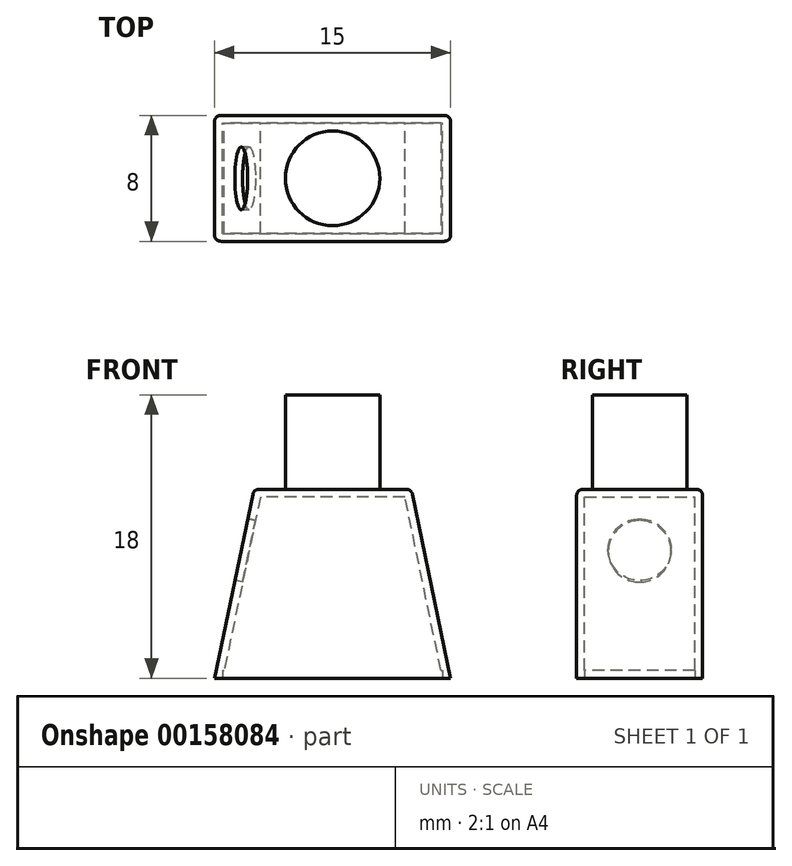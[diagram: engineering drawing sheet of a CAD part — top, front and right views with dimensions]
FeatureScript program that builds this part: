
annotation { "Feature Type Name" : "Feature", "Feature Type Description" : "" }
export const myFeature = defineFeature(function(context is Context, id is Id, definition is map)
    precondition{}
    {
        {
            var Q0;
            Q0=qCreatedBy(makeId("Front.planeOp"),FACE);
            var sketch = newSketch(context, id + "F0", { "sketchPlane" : qUnion([Q0])});
            skLineSegment(sketch, "E0", {"start": v(0, 0) * mm, "end": v(7.5, 0) * mm});
            skLineSegment(sketch, "E1", {"start": v(7.5, 0) * mm, "end": v(5, 12) * mm});
            skLineSegment(sketch, "E2", {"start": v(5, 12) * mm, "end": v(0, 12) * mm});
            skLineSegment(sketch, "E3", {"start": v(0, 12) * mm, "end": v(-5, 12) * mm});
            skLineSegment(sketch, "E4", {"start": v(-5, 12) * mm, "end": v(-7.5, 0) * mm});
            skLineSegment(sketch, "E5", {"start": v(-7.5, 0) * mm, "end": v(0, 0) * mm});
            skSolve(sketch);
        }
        {
            var Q0;
            Q0=makeQuery(id+"F0.imprint","IMPRINT",FACE,{"disambiguationData":[TD([[makeQuery(id+"F0.imprint","IMPRINT",EDGE,{"derivedFrom":sQuery(id+"F0.wireOp",EDGE,"E0")}),1.0]])]});
            extrude(context, id + "F1", {"entities" : qUnion([Q0]), "depth" : 8 * mm});
        }
        {
            var Q0;
            Q0=makeQuery(id+"F1.opExtrude","SWEPT_FACE",FACE,{"disambiguationData":[OSD([sQuery(id+"F0.wireOp",EDGE,"E0"),sQuery(id+"F0.wireOp",EDGE,"E5")])]});
            shell(context, id + "F2", {"entities" : qUnion([Q0]), "thickness" : 0.5 * mm});
        }
        {
            var Q0;
            Q0=makeQuery(id+"F1.opExtrude","SWEPT_FACE",FACE,{"disambiguationData":[OSD([sQuery(id+"F0.wireOp",EDGE,"E0"),sQuery(id+"F0.wireOp",EDGE,"E5")])]});
            var sketch = newSketch(context, id + "F3", { "sketchPlane" : qUnion([Q0])});
            skLineSegment(sketch, "E6.0", {"start": v(-6.99, 7.5) * mm, "end": v(6.99, 7.5) * mm});
            skLineSegment(sketch, "E7.0", {"start": v(-6.99, 7.5) * mm, "end": v(-6.99, 0.5) * mm});
            skLineSegment(sketch, "E8.0", {"start": v(-6.99, 0.5) * mm, "end": v(6.99, 0.5) * mm});
            skLineSegment(sketch, "E9.0", {"start": v(6.99, 7.5) * mm, "end": v(6.99, 0.5) * mm});
            skSolve(sketch);
        }
        {
            var Q0;
            Q0=makeQuery(id+"F3.imprint","IMPRINT",FACE,{"disambiguationData":[TD([[makeQuery(id+"F3.imprint","IMPRINT",EDGE,{"derivedFrom":sQuery(id+"F3.wireOp",EDGE,"E6.0")}),-1.0]])]});
            extrude(context, id + "F4", {"entities" : qUnion([Q0]), "operationType" : NewBodyOperationType.REMOVE, "oppositeDirection" : true, "depth" : 0.5 * mm});
        }
        {
            var Q0;
            Q0=makeQuery(id+"F1.opExtrude","CAP_EDGE",EDGE,{"disambiguationData":[OSD([sQuery(id+"F0.wireOp",EDGE,"E1")])],"isStart":false});
            var Q1;
            Q1=makeQuery(id+"F1.opExtrude","SWEPT_EDGE",EDGE,{"disambiguationData":[OSD([sQuery(id+"F0.wireOp",EDGE,"E1"),sQuery(id+"F0.wireOp",EDGE,"E2")])]});
            var Q2;
            Q2=makeQuery(id+"F1.opExtrude","CAP_EDGE",EDGE,{"disambiguationData":[OSD([sQuery(id+"F0.wireOp",EDGE,"E2"),sQuery(id+"F0.wireOp",EDGE,"E3")])],"isStart":false});
            var Q3;
            Q3=makeQuery(id+"F1.opExtrude","CAP_EDGE",EDGE,{"disambiguationData":[OSD([sQuery(id+"F0.wireOp",EDGE,"E1")])],"isStart":true});
            var Q4;
            Q4=makeQuery(id+"F1.opExtrude","CAP_EDGE",EDGE,{"disambiguationData":[OSD([sQuery(id+"F0.wireOp",EDGE,"E2"),sQuery(id+"F0.wireOp",EDGE,"E3")])],"isStart":true});
            var Q5;
            Q5=makeQuery(id+"F1.opExtrude","CAP_EDGE",EDGE,{"disambiguationData":[OSD([sQuery(id+"F0.wireOp",EDGE,"E4")])],"isStart":true});
            var Q6;
            Q6=makeQuery(id+"F1.opExtrude","SWEPT_EDGE",EDGE,{"disambiguationData":[OSD([sQuery(id+"F0.wireOp",EDGE,"E3"),sQuery(id+"F0.wireOp",EDGE,"E4")])]});
            var Q7;
            Q7=makeQuery(id+"F1.opExtrude","CAP_EDGE",EDGE,{"disambiguationData":[OSD([sQuery(id+"F0.wireOp",EDGE,"E4")])],"isStart":false});
            fillet(context, id + "F5", {"entities" : qUnion([Q0, Q1, Q2, Q3, Q4, Q5, Q6, Q7]), "radius" : 0.4 * mm, "tangentPropagation" : true, "allowEdgeOverflow" : false});
        }
        {
            var Q0;
            Q0=makeQuery(id+"F1.opExtrude","SWEPT_FACE",FACE,{"disambiguationData":[OSD([sQuery(id+"F0.wireOp",EDGE,"E4")])]});
            var sketch = newSketch(context, id + "F6", { "sketchPlane" : qUnion([Q0])});
            skCircle(sketch, "E10", {"center": v(4, 6.8) * mm, "radius": 2 * mm});
            skSolve(sketch);
        }
        {
            var Q0;
            Q0=makeQuery(id+"F6.imprint","IMPRINT",FACE,{"disambiguationData":[TD([[makeQuery(id+"F6.imprint","IMPRINT",EDGE,{"derivedFrom":sQuery(id+"F6.wireOp",EDGE,"E10")}),1.0]])]});
            extrude(context, id + "F7", {"entities" : qUnion([Q0]), "operationType" : NewBodyOperationType.REMOVE, "oppositeDirection" : true, "depth" : 1 * mm});
        }
        {
            var Q0;
            Q0=makeQuery(id+"F1.opExtrude","SWEPT_FACE",FACE,{"disambiguationData":[OSD([sQuery(id+"F0.wireOp",EDGE,"E2"),sQuery(id+"F0.wireOp",EDGE,"E3")])]});
            var sketch = newSketch(context, id + "F8", { "sketchPlane" : qUnion([Q0])});
            skCircle(sketch, "E11", {"center": v(0, -4) * mm, "radius": 3 * mm});
            skSolve(sketch);
        }
        {
            var Q0;
            Q0=makeQuery(id+"F8.imprint","IMPRINT",FACE,{"disambiguationData":[TD([[makeQuery(id+"F8.imprint","IMPRINT",EDGE,{"derivedFrom":sQuery(id+"F8.wireOp",EDGE,"E11")}),1.0]])]});
            extrude(context, id + "F9", {"entities" : qUnion([Q0]), "operationType" : NewBodyOperationType.ADD, "depth" : 6 * mm});
        }
    });
